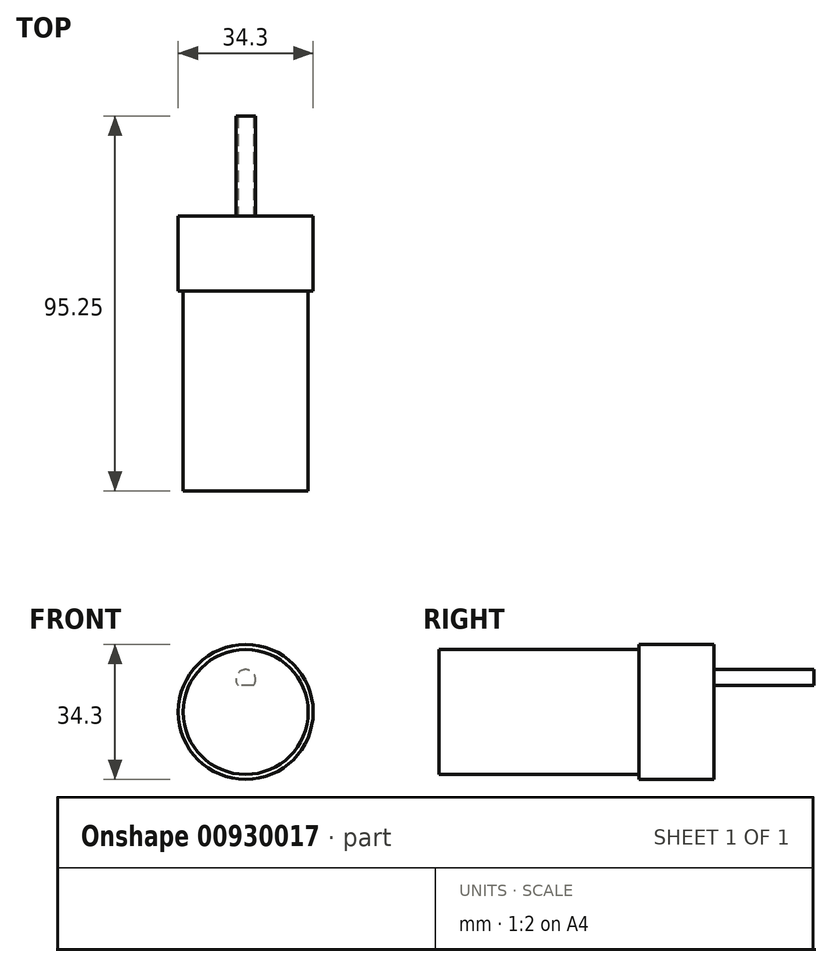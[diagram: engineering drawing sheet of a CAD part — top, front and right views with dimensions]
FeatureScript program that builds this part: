
annotation { "Feature Type Name" : "Feature", "Feature Type Description" : "" }
export const myFeature = defineFeature(function(context is Context, id is Id, definition is map)
    precondition{}
    {
        {
            var Q0;
            Q0=qCreatedBy(makeId("Front.planeOp"),FACE);
            var sketch = newSketch(context, id + "F0", { "sketchPlane" : qUnion([Q0])});
            skCircle(sketch, "E0", {"center": v(0, 0) * mm, "radius": 17.14 * mm});
            skSolve(sketch);
        }
        {
            var Q0;
            Q0 = qSketchRegion(id + "F0", true);
            extrude(context, id + "F1", {"entities" : qUnion([Q0]), "depth" : 19.05 * mm, "offsetDistance" : 25.4 * mm});
        }
        {
            var Q0;
            Q0=makeQuery(id+"F1.opExtrude","CAP_FACE",FACE,{"disambiguationData":[OSD([sQuery(id+"F0.wireOp",EDGE,"E0")])],"isStart":true});
            var sketch = newSketch(context, id + "F2", { "sketchPlane" : qUnion([Q0])});
            skLineSegment(sketch, "E1", {"start": v(0, -17.15) * mm, "end": v(0, 8.25) * mm, "construction": true});
            skArc(sketch, "E2", {"start": v(1.98, 6.73) * mm, "mid": v(0, 10.75) * mm, "end": v(-1.98, 6.73) * mm});
            skLineSegment(sketch, "E3", {"start": v(0, 8.25) * mm, "end": v(0, 9.78) * mm, "construction": true});
            skLineSegment(sketch, "E4", {"start": v(-2.5, 8.25) * mm, "end": v(2.5, 8.25) * mm, "construction": true});
            skLineSegment(sketch, "E5.MirrorCS", {"start": v(-1.98, 6.73) * mm, "end": v(1.98, 6.73) * mm});
            skPoint(sketch, "E6.orphan", {"position": v(1.98, 9.78) * mm});
            skPoint(sketch, "E7.start.orphan", {"position": v(-1.98, 9.78) * mm});
            skSolve(sketch);
        }
        {
            var Q0;
            Q0 = qSketchRegion(id + "F2", true);
            extrude(context, id + "F3", {"entities" : qUnion([Q0]), "operationType" : NewBodyOperationType.ADD, "depth" : 25.4 * mm, "offsetDistance" : 25.4 * mm});
        }
        {
            var Q0;
            Q0=makeQuery(id+"F1.opExtrude","CAP_FACE",FACE,{"disambiguationData":[OSD([sQuery(id+"F0.wireOp",EDGE,"E0")])],"isStart":false});
            var sketch = newSketch(context, id + "F4", { "sketchPlane" : qUnion([Q0])});
            skCircle(sketch, "E8", {"center": v(0, 0) * mm, "radius": 15.88 * mm});
            skSolve(sketch);
        }
        {
            var Q0;
            Q0 = qSketchRegion(id + "F4", true);
            extrude(context, id + "F5", {"entities" : qUnion([Q0]), "operationType" : NewBodyOperationType.ADD, "depth" : 50.8 * mm, "offsetDistance" : 25.4 * mm});
        }
    });
